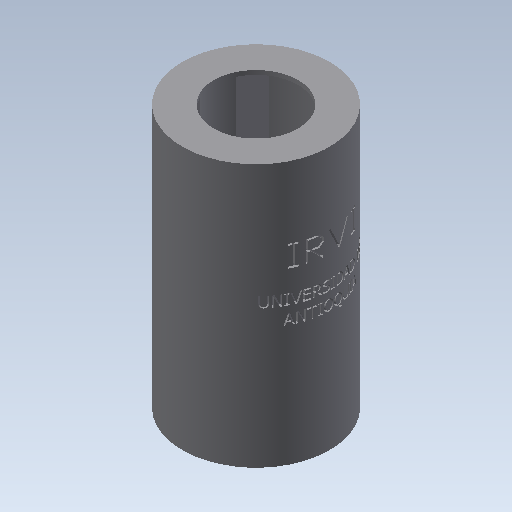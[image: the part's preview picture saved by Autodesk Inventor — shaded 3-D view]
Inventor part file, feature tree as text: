
AUTODESK INVENTOR PART (.ipt)
format: ipt  version: 2021.3 (Build 253353010, 353A)  size: 1,083,904 bytes
history: native  units: mm
features: sketch x8, extrude x6, emboss x3, plane x2, mirror x1
ambient origin geometry x8: Origin, YZ Plane, XZ Plane, XY Plane, X Axis, Y Axis, Z Axis, Center Point
bodies: Solid1 (feature_tree)
feature tree (20):
  extrude  "Extrusion1"  Depth=125.0mm TaperAngle=0.0deg
  extrude  "Extrusion2"  Depth=123.0mm TaperAngle=0.0deg
  plane  "Work Plane1"
  plane  "Work Plane2"
  extrude  "Extrusion3"  Depth=43.046mm
  mirror  "Mirror1"
  extrude  "Extrusion4"  Depth=40.0mm
  emboss  "Emboss1"
  sketch  "Sketch7"  dims[d29=12.0mm d30=0.0mm d31=2.0mm d32=0.0mm]
  emboss  "Emboss2"
  emboss  "Emboss3"
  extrude  "Extrusion7"  Depth=2.0mm TaperAngle=0.0deg
  extrude  "Extrusion8"  Depth=2.0mm TaperAngle=0.0deg
  sketch  "Sketch1"  dims[d0=70.0mm d1=125.0mm d2=0.0mm]
  sketch  "Sketch2"  dims[d3=67.0mm d4=123.0mm d5=0.0mm]
  sketch  "Sketch3"  dims[d6=20.0mm d7=-20.0mm d8=43.046mm]
  sketch  "Sketch4"  dims[d9=2.0mm d10=0.0mm d11=40.0mm]
  sketch  "Sketch6"  dims[d12=0.0mm d13=0.0mm d27=2.0mm d28=0.0mm]
  sketch  "Sketch9"  dims[d35=2.727mm]
  sketch  "Sketch10"  dims[d37=2.727mm d38=0.0mm d39=0.0mm d40=2.727mm d41=2.727mm d42=2.727mm d43=0.0mm d44=0.0mm]
